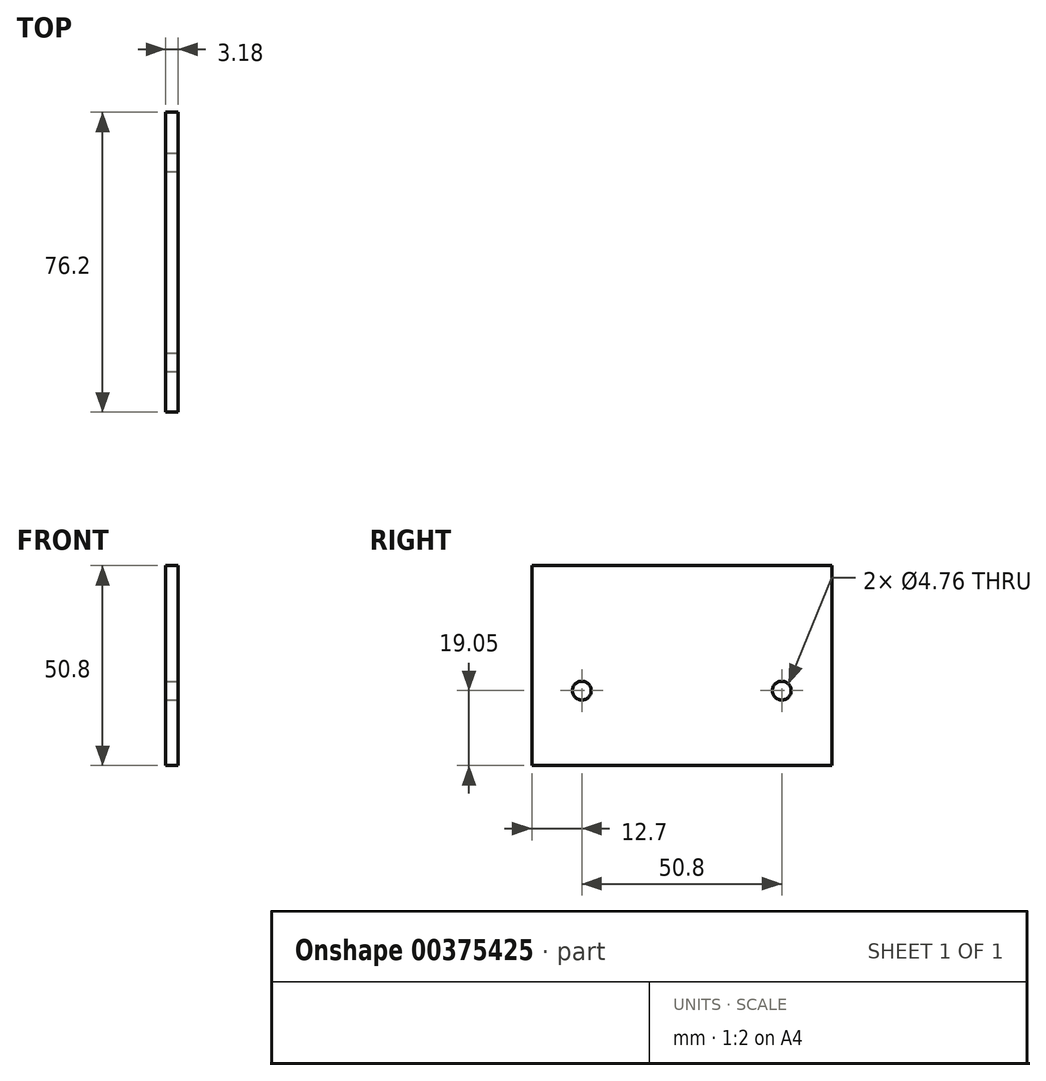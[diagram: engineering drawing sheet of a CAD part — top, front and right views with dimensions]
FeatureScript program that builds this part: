
annotation { "Feature Type Name" : "Feature", "Feature Type Description" : "" }
export const myFeature = defineFeature(function(context is Context, id is Id, definition is map)
    precondition{}
    {
        {
            var Q0;
            Q0=qCreatedBy(makeId("Front.planeOp"),FACE);
            var sketch = newSketch(context, id + "F0", { "sketchPlane" : qUnion([Q0])});
            skLineSegment(sketch, "E0.bottom", {"start": v(1.59, 25.4) * mm, "end": v(-1.59, 25.4) * mm});
            skLineSegment(sketch, "E0.top", {"start": v(1.59, -25.4) * mm, "end": v(-1.59, -25.4) * mm});
            skLineSegment(sketch, "E0.left", {"start": v(1.59, 25.4) * mm, "end": v(1.59, -25.4) * mm});
            skLineSegment(sketch, "E0.right", {"start": v(-1.59, 25.4) * mm, "end": v(-1.59, -25.4) * mm});
            skPoint(sketch, "E0.middle", {"position": v(0, 0) * mm});
            skSolve(sketch);
        }
        {
            var Q0;
            Q0=qSketchRegion(id+"F0",true);
            extrude(context, id + "F1", {"entities" : qUnion([Q0]), "depth" : 76.2 * mm, "symmetric" : true});
        }
        {
            var Q0;
            Q0=makeQuery(id+"F1.opExtrude","SWEPT_FACE",FACE,{"disambiguationData":[OSD([sQuery(id+"F0.wireOp",EDGE,"E0.left")])]});
            var sketch = newSketch(context, id + "F2", { "sketchPlane" : qUnion([Q0])});
            skCircle(sketch, "E1", {"center": v(25.4, -6.35) * mm, "radius": 2.38 * mm});
            skCircle(sketch, "E2", {"center": v(-25.4, -6.35) * mm, "radius": 2.38 * mm});
            skSolve(sketch);
        }
        {
            var Q0;
            Q0=qSketchRegion(id+"F2",true);
            extrude(context, id + "F3", {"entities" : qUnion([Q0]), "operationType" : NewBodyOperationType.REMOVE, "oppositeDirection" : true, "depth" : 25.4 * mm});
        }
    });
